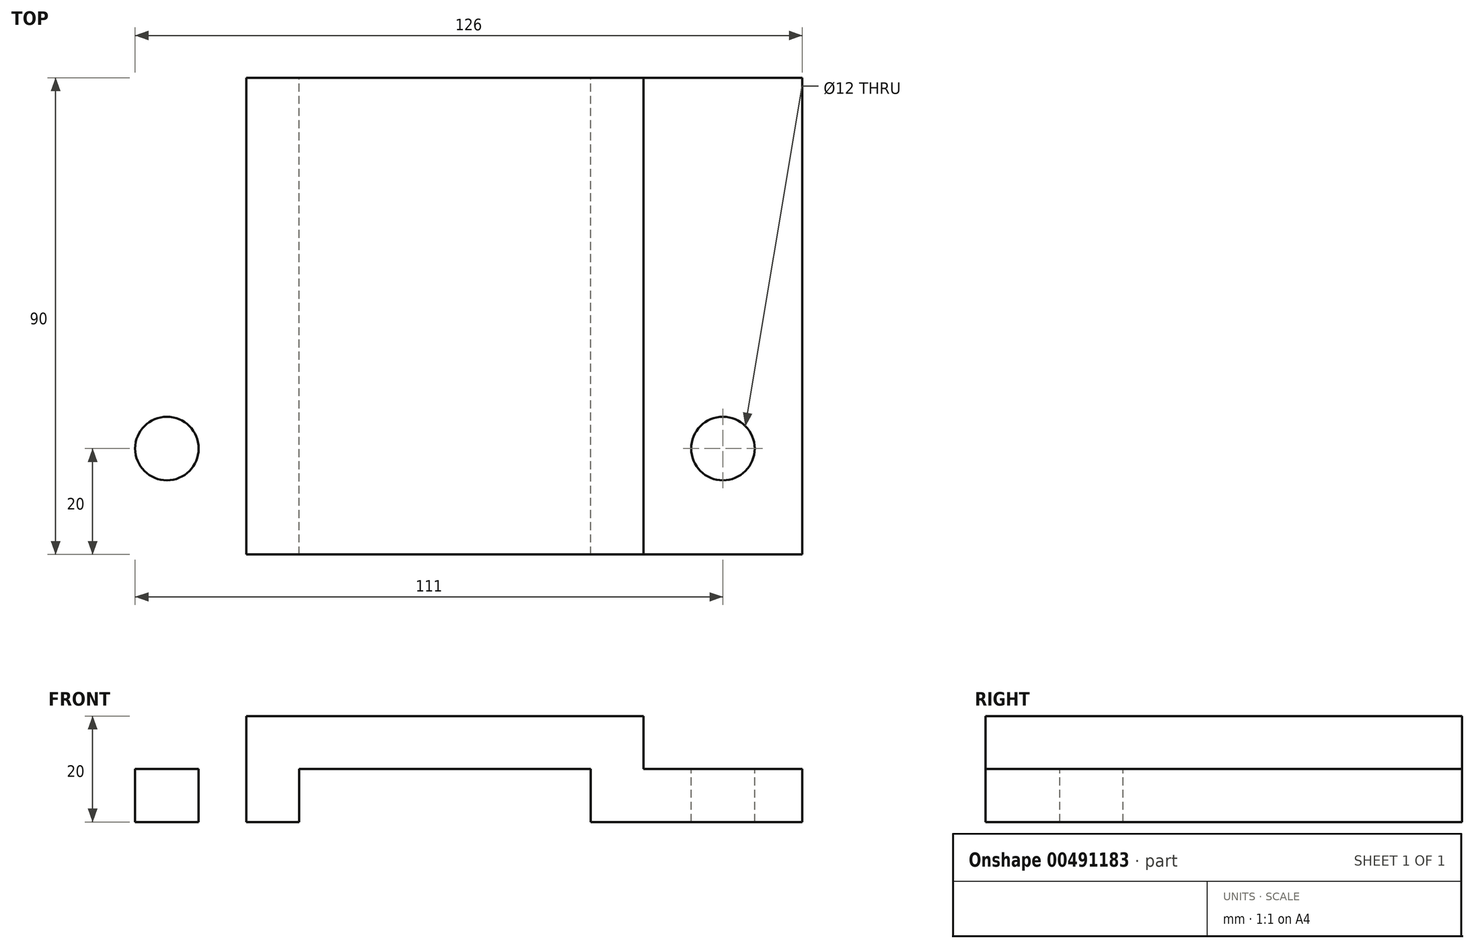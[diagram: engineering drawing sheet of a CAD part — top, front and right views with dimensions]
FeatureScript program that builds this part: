
annotation { "Feature Type Name" : "Feature", "Feature Type Description" : "" }
export const myFeature = defineFeature(function(context is Context, id is Id, definition is map)
    precondition{}
    {
        {
            var Q0;
            Q0=qCreatedBy(makeId("Front.planeOp"),FACE);
            var sketch = newSketch(context, id + "F0", { "sketchPlane" : qUnion([Q0])});
            skLineSegment(sketch, "E0", {"start": v(0, 20) * mm, "end": v(0, 10) * mm});
            skLineSegment(sketch, "E1", {"start": v(0, 10) * mm, "end": v(27.5, 10) * mm});
            skLineSegment(sketch, "E2", {"start": v(27.5, 10) * mm, "end": v(27.5, 0) * mm});
            skLineSegment(sketch, "E3", {"start": v(27.5, 0) * mm, "end": v(67.5, 0) * mm});
            skLineSegment(sketch, "E4", {"start": v(67.5, 0) * mm, "end": v(67.5, 10) * mm});
            skLineSegment(sketch, "E5", {"start": v(67.5, 10) * mm, "end": v(37.5, 10) * mm});
            skLineSegment(sketch, "E6", {"start": v(37.5, 10) * mm, "end": v(37.5, 20) * mm});
            skLineSegment(sketch, "E7", {"start": v(37.5, 20) * mm, "end": v(0, 20) * mm});
            skLineSegment(sketch, "E8.MirrorCS", {"start": v(-67.5, 0) * mm, "end": v(-67.5, 10) * mm});
            skLineSegment(sketch, "E9.MirrorCS", {"start": v(-67.5, 10) * mm, "end": v(-37.5, 10) * mm});
            skLineSegment(sketch, "E10.MirrorCS", {"start": v(-27.5, 0) * mm, "end": v(-67.5, 0) * mm});
            skLineSegment(sketch, "E11.MirrorCS", {"start": v(-27.5, 10) * mm, "end": v(-27.5, 0) * mm});
            skLineSegment(sketch, "E12.MirrorCS", {"start": v(-37.5, 20) * mm, "end": v(0, 20) * mm});
            skLineSegment(sketch, "E13.MirrorCS", {"start": v(-37.5, 10) * mm, "end": v(-37.5, 20) * mm});
            skLineSegment(sketch, "E14.MirrorCS", {"start": v(0, 10) * mm, "end": v(-27.5, 10) * mm});
            skSolve(sketch);
        }
        {
            var Q0;
            Q0=makeQuery(id+"F0.imprint","IMPRINT",FACE,{"disambiguationData":[TD([[makeQuery(id+"F0.imprint","IMPRINT",EDGE,{"derivedFrom":sQuery(id+"F0.wireOp",EDGE,"E0")}),-1.0]])]});
            var Q1;
            Q1=makeQuery(id+"F0.imprint","IMPRINT",FACE,{"disambiguationData":[TD([[makeQuery(id+"F0.imprint","IMPRINT",EDGE,{"derivedFrom":sQuery(id+"F0.wireOp",EDGE,"E0")}),1.0]])]});
            extrude(context, id + "F1", {"entities" : qUnion([Q0, Q1]), "depth" : 90 * mm, "symmetric" : true});
        }
        {
            var Q0;
            Q0=makeQuery(id+"F1.opExtrude","SWEPT_FACE",FACE,{"disambiguationData":[OSD([sQuery(id+"F0.wireOp",EDGE,"E9.MirrorCS")])]});
            var sketch = newSketch(context, id + "F2", { "sketchPlane" : qUnion([Q0])});
            skCircle(sketch, "E15", {"center": v(-52.5, 25) * mm, "radius": 6 * mm});
            skCircle(sketch, "E16.MirrorC", {"center": v(52.5, 25) * mm, "radius": 6 * mm});
            skCircle(sketch, "E17.MirrorC", {"center": v(-52.5, -25) * mm, "radius": 6 * mm});
            skCircle(sketch, "E18.MirrorC", {"center": v(52.5, -25) * mm, "radius": 6 * mm});
            skSolve(sketch);
        }
        {
            var Q0;
            Q0=makeQuery(id+"F2.imprint","IMPRINT",FACE,{"disambiguationData":[TD([[makeQuery(id+"F2.imprint","IMPRINT",EDGE,{"derivedFrom":sQuery(id+"F2.wireOp",EDGE,"E15")}),1.0]])]});
            var Q1;
            Q1=makeQuery(id+"F2.imprint","IMPRINT",FACE,{"disambiguationData":[TD([[makeQuery(id+"F2.imprint","IMPRINT",EDGE,{"derivedFrom":sQuery(id+"F2.wireOp",EDGE,"E16.MirrorC")}),-1.0]])]});
            var Q2;
            Q2=makeQuery(id+"F2.imprint","IMPRINT",FACE,{"disambiguationData":[TD([[makeQuery(id+"F2.imprint","IMPRINT",EDGE,{"derivedFrom":sQuery(id+"F2.wireOp",EDGE,"E18.MirrorC")}),1.0]])]});
            var Q3;
            Q3=makeQuery(id+"F2.imprint","IMPRINT",FACE,{"disambiguationData":[TD([[makeQuery(id+"F2.imprint","IMPRINT",EDGE,{"derivedFrom":sQuery(id+"F2.wireOp",EDGE,"E17.MirrorC")}),-1.0]])]});
            extrude(context, id + "F3", {"entities" : qUnion([Q0, Q1, Q2, Q3]), "operationType" : NewBodyOperationType.REMOVE, "endBound" : BoundingType.THROUGH_ALL, "oppositeDirection" : true, "depth" : 25 * mm});
        }
    });
